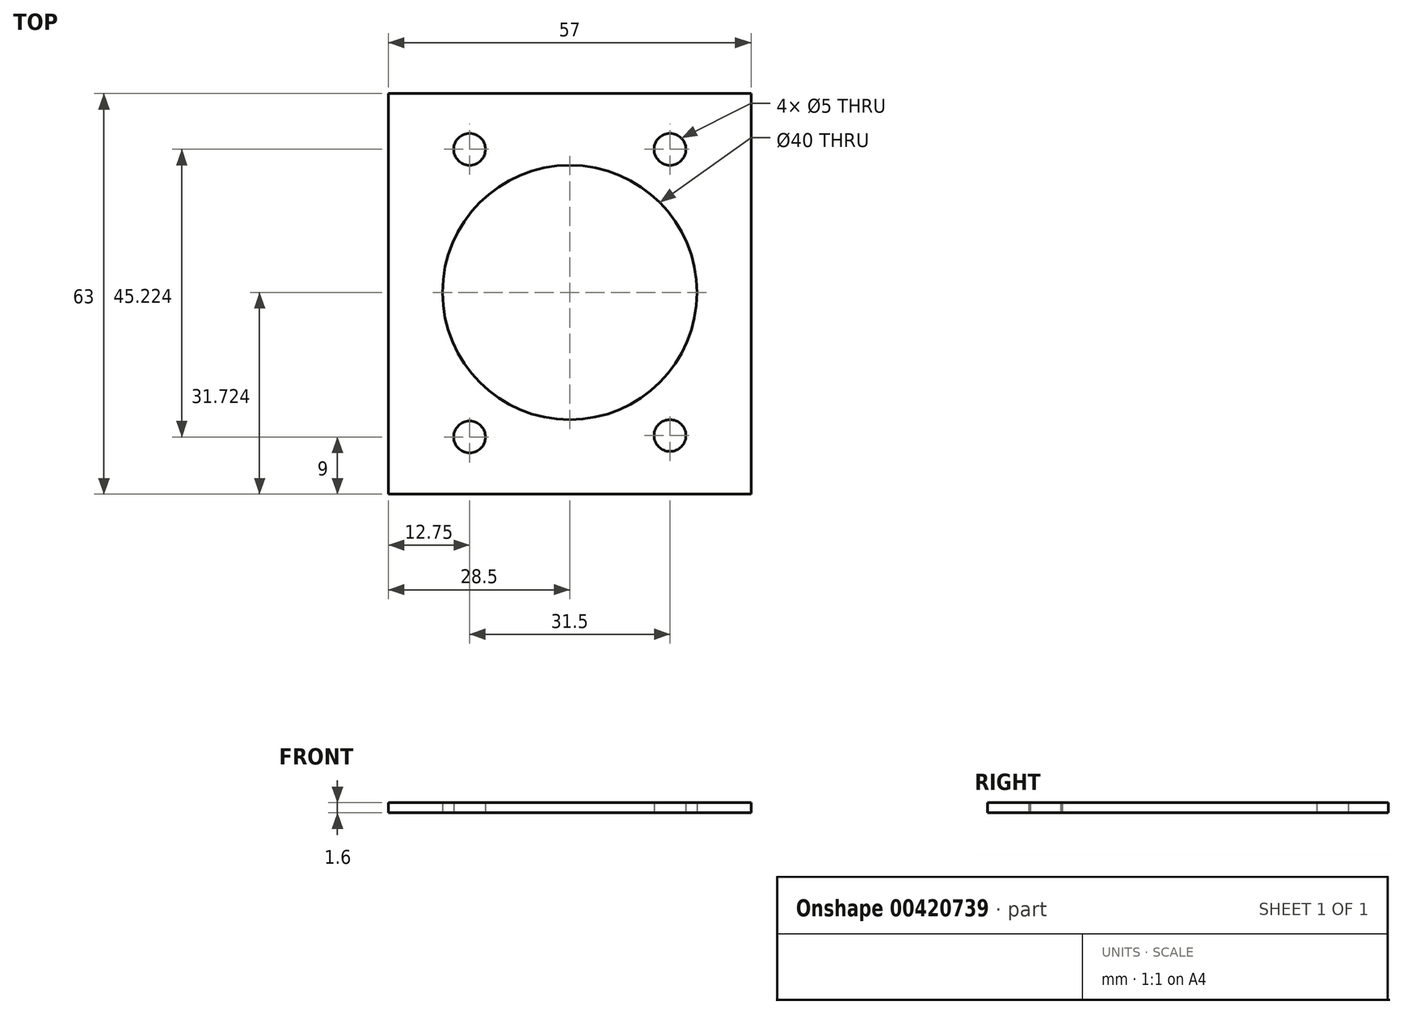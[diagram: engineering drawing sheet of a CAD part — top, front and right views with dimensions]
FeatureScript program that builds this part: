
annotation { "Feature Type Name" : "Feature", "Feature Type Description" : "" }
export const myFeature = defineFeature(function(context is Context, id is Id, definition is map)
    precondition{}
    {
        {
            var Q0;
            Q0=qCreatedBy(makeId("Top.planeOp"),FACE);
            var sketch = newSketch(context, id + "F0", { "sketchPlane" : qUnion([Q0])});
            skLineSegment(sketch, "E0.bottom", {"start": v(0, 0) * mm, "end": v(-57, 0) * mm});
            skLineSegment(sketch, "E0.top", {"start": v(0, 63) * mm, "end": v(-57, 63) * mm});
            skLineSegment(sketch, "E0.left", {"start": v(0, 0) * mm, "end": v(0, 63) * mm});
            skLineSegment(sketch, "E0.right", {"start": v(-57, 0) * mm, "end": v(-57, 63) * mm});
            skLineSegment(sketch, "E1", {"start": v(-4, 54.22) * mm, "end": v(-53, 54.22) * mm});
            skLineSegment(sketch, "E2", {"start": v(-28.5, 54.22) * mm, "end": v(-12.75, 54.22) * mm});
            skCircle(sketch, "E3", {"center": v(-12.75, 54.22) * mm, "radius": 2.5 * mm});
            skLineSegment(sketch, "E4", {"start": v(-28.5, 54.22) * mm, "end": v(-28.5, 31.72) * mm});
            skLineSegment(sketch, "E5", {"start": v(-30.3, 31.72) * mm, "end": v(-28.5, 31.72) * mm});
            skCircle(sketch, "E6.MirrorC", {"center": v(-12.75, 9.22) * mm, "radius": 2.5 * mm});
            skCircle(sketch, "E7.MirrorC", {"center": v(-44.25, 9) * mm, "radius": 2.5 * mm});
            skLineSegment(sketch, "E8", {"start": v(-44.25, 9) * mm, "end": v(-57, 9) * mm});
            skLineSegment(sketch, "E9", {"start": v(-44.25, 9) * mm, "end": v(-44.25, 0) * mm});
            skCircle(sketch, "E10", {"center": v(-44.25, 54.22) * mm, "radius": 2.5 * mm});
            skCircle(sketch, "E11", {"center": v(-28.5, 31.72) * mm, "radius": 20 * mm});
            skSolve(sketch);
        }
        {
            var Q0;
            Q0=qSketchRegion(id+"F0",true);
            extrude(context, id + "F1", {"entities" : qUnion([Q0]), "depth" : 1.6 * mm});
        }
    });
